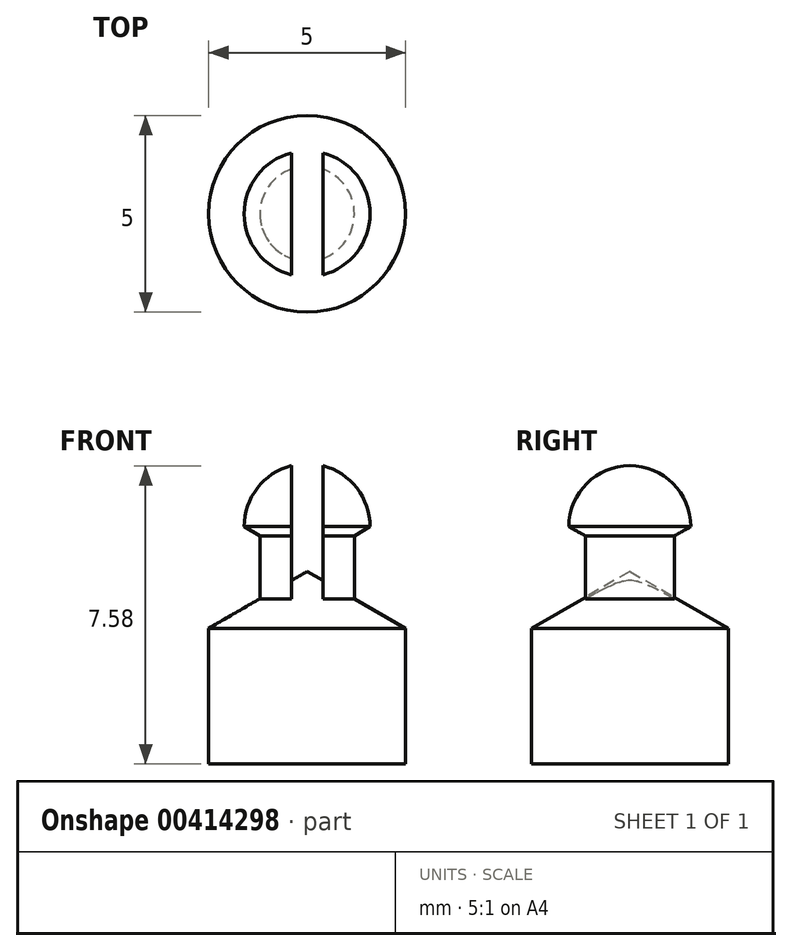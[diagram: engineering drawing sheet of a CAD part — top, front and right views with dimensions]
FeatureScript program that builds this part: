
annotation { "Feature Type Name" : "Feature", "Feature Type Description" : "" }
export const myFeature = defineFeature(function(context is Context, id is Id, definition is map)
    precondition{}
    {
        {
            var Q0;
            Q0=qCreatedBy(makeId("Front.planeOp"),FACE);
            var sketch = newSketch(context, id + "F0", { "sketchPlane" : qUnion([Q0])});
            skLineSegment(sketch, "E0", {"start": v(0, 0) * mm, "end": v(-2.5, 0) * mm});
            skLineSegment(sketch, "E1", {"start": v(-2.5, 0) * mm, "end": v(-2.5, 3.45) * mm});
            skLineSegment(sketch, "E2", {"start": v(-2.5, 3.45) * mm, "end": v(-1.2, 4.2) * mm});
            skLineSegment(sketch, "E3", {"start": v(-1.2, 4.2) * mm, "end": v(-1.2, 5.8) * mm});
            skLineSegment(sketch, "E4", {"start": v(-1.2, 5.8) * mm, "end": v(-1.6, 6.03) * mm});
            skArc(sketch, "E5", {"start": v(-1.6, 6.03) * mm, "mid": v(-1.13, 7.16) * mm, "end": v(0, 7.63) * mm});
            skLineSegment(sketch, "E6", {"start": v(0, 7.63) * mm, "end": v(0, 0) * mm});
            skPoint(sketch, "E7", {"position": v(-1.2, 5) * mm});
            skSolve(sketch);
        }
        {
            var Q0;
            Q0=makeQuery(id+"F0.imprint","IMPRINT",FACE,{"disambiguationData":[TD([[makeQuery(id+"F0.imprint","IMPRINT",EDGE,{"derivedFrom":sQuery(id+"F0.wireOp",EDGE,"E0")}),-1.0]])]});
            var Q1;
            Q1=sQuery(id+"F0.wireOp",EDGE,"E6");
            revolve(context, id + "F1", {"entities" : qUnion([Q0]), "axis" : qUnion([Q1]), "revolveType" : RevolveType.FULL});
        }
        {
            var Q0;
            Q0=qCreatedBy(makeId("Top.planeOp"),FACE);
            cPlane(context, id + "F2", {"entities" : qUnion([Q0]), "cplaneType" : CPlaneType.OFFSET, "offset" : 25.4 * mm, "width" : 152.4 * mm, "height" : 152.4 * mm});
        }
        {
            var Q0;
            Q0=qCreatedBy(id+"F2.planeOp",FACE);
            var sketch = newSketch(context, id + "F3", { "sketchPlane" : qUnion([Q0])});
            skLineSegment(sketch, "E8.bottom", {"start": v(0.4, 1.6) * mm, "end": v(-0.4, 1.6) * mm});
            skLineSegment(sketch, "E8.top", {"start": v(0.4, -1.6) * mm, "end": v(-0.4, -1.6) * mm});
            skLineSegment(sketch, "E8.left", {"start": v(0.4, 1.6) * mm, "end": v(0.4, -1.6) * mm});
            skLineSegment(sketch, "E8.right", {"start": v(-0.4, 1.6) * mm, "end": v(-0.4, -1.6) * mm});
            skPoint(sketch, "E8.middle", {"position": v(0, 0) * mm});
            skSolve(sketch);
        }
        {
            var Q0;
            Q0=makeQuery(id+"F3.imprint","IMPRINT",FACE,{"disambiguationData":[TD([[makeQuery(id+"F3.imprint","IMPRINT",EDGE,{"derivedFrom":sQuery(id+"F3.wireOp",EDGE,"E8.bottom")}),1.0]])]});
            var Q1;
            Q1=makeQuery(id+"F1.opRevolve","SWEPT_FACE",FACE,{"disambiguationData":[OSD([sQuery(id+"F0.wireOp",EDGE,"E2")])]});
            extrude(context, id + "F4", {"entities" : qUnion([Q0]), "operationType" : NewBodyOperationType.REMOVE, "endBound" : BoundingType.UP_TO_SURFACE, "oppositeDirection" : true, "endBoundEntityFace" : qUnion([Q1]), "depth" : 25.4 * mm});
        }
    });
